# Revit family: ancoPLUS
name_source: partatom
category: Fixadores estruturais
revit_build: Autodesk Revit 2018 (Build: 20180423_1000(x64)
units: mm (PartAtom-declared; Revit-internal decimal feet)

## family parameters
Com base no plano de trabalho = Não
Compartilhado = Não
Corte com vazios quando carregada = Não
Sempre na vertical = Sim

## types (12) — shared parameters
Ancre_hauteur = 100  [stored 0.328084 ft]
Fers de montage inférieur = Sim
Fers de montage supérieur = Sim
LT1 = 1100
LT2 = 1050
Longueur fers de montage après dernière ancre = 100  [stored 0.328084 ft]
Material = Ancre
Nombre d’ancres = 10
Visibilidade_Acre_10 = Sim
Visibilidade_Acre_2 = Sim
Visibilidade_Acre_3 = Sim
Visibilidade_Acre_4 = Sim
Visibilidade_Acre_5 = Sim
Visibilidade_Acre_6 = Sim
Visibilidade_Acre_7 = Sim
Visibilidade_Acre_8 = Sim
Visibilidade_Acre_9 = Sim
XC1 = 100  [stored 0.328084 ft]
XC10 = 100  [stored 0.328084 ft]
XC2 = 100  [stored 0.328084 ft]
XC3 = 100  [stored 0.328084 ft]
XC4 = 100  [stored 0.328084 ft]
XC5 = 100  [stored 0.328084 ft]
XC6 = 100  [stored 0.328084 ft]
XC7 = 100  [stored 0.328084 ft]
XC8 = 100  [stored 0.328084 ft]
XC9 = 100  [stored 0.328084 ft]

## per-type parameters (varying)
| type | Ancre_Ø | Ancre_Ø/2 | Enrobage supérieure | H1 | H2 | H_T | Modelo | Ø | ØF | ØF_Posição_Horizontal | ØF_Posição_Vertical | ØT |
| DX | 10 | 5  [stored 0.0164042 ft] | 0  [stored 0 ft] | 3  [stored 0.00984252 ft] | 3  [stored 0.00984252 ft] | 88 | DX | 10  [stored 0.0328084 ft] | 6  [stored 0.019685 ft] | 9  [stored 0.0295276 ft] | 3  [stored 0.00984252 ft] | 15  [stored 0.0492126 ft] |
| DA | 12 | 6  [stored 0.019685 ft] | 80  [stored 0.262467 ft] | 3  [stored 0.00984252 ft] | 3  [stored 0.00984252 ft] | 87 | DA | 12  [stored 0.0393701 ft] | 6  [stored 0.019685 ft] | 9  [stored 0.0295276 ft] | 3  [stored 0.00984252 ft] | 18  [stored 0.0590551 ft] |
| DB | 14 | 7  [stored 0.0229659 ft] | 80  [stored 0.262467 ft] | 4  [stored 0.0131234 ft] | 4  [stored 0.0131234 ft] | 86  [stored 0.282152 ft] | DB | 14  [stored 0.0459318 ft] | 6  [stored 0.019685 ft] | 9  [stored 0.0295276 ft] | 3  [stored 0.00984252 ft] | 21  [stored 0.0688976 ft] |
| DC | 16 | 8  [stored 0.0262467 ft] | 80  [stored 0.262467 ft] | 4  [stored 0.0131234 ft] | 4  [stored 0.0131234 ft] | 86  [stored 0.282152 ft] | DC | 16  [stored 0.0524934 ft] | 8  [stored 0.0262467 ft] | 10  [stored 0.0328084 ft] | 4  [stored 0.0131234 ft] | 24  [stored 0.0787402 ft] |
| DG | 20 | 10  [stored 0.0328084 ft] | 80  [stored 0.262467 ft] | 4  [stored 0.0131234 ft] | 5  [stored 0.0164042 ft] | 82  [stored 0.269029 ft] | DG | 20  [stored 0.0656168 ft] | 9  [stored 0.0295276 ft] | 11  [stored 0.0360892 ft] | 5  [stored 0.0164042 ft] | 30  [stored 0.0984252 ft] |
| DJ | 22 | 11  [stored 0.0360892 ft] | 80  [stored 0.262467 ft] | 5  [stored 0.0164042 ft] | 6  [stored 0.019685 ft] | 80  [stored 0.262467 ft] | DJ | 22  [stored 0.0721785 ft] | 8  [stored 0.0262467 ft] | 10  [stored 0.0328084 ft] | 4  [stored 0.0131234 ft] | 33 |
| DO | 25 | 13 | 80  [stored 0.262467 ft] | 6  [stored 0.019685 ft] | 7  [stored 0.0229659 ft] | 74  [stored 0.242782 ft] | DO | 25  [stored 0.082021 ft] | 10  [stored 0.0328084 ft] | 11  [stored 0.0360892 ft] | 5  [stored 0.0164042 ft] | 38 |
| DN | 25 | 13 | 80  [stored 0.262467 ft] | 6  [stored 0.019685 ft] | 7  [stored 0.0229659 ft] | 74  [stored 0.242782 ft] | DO | 25  [stored 0.082021 ft] | 10  [stored 0.0328084 ft] | 11  [stored 0.0360892 ft] | 5  [stored 0.0164042 ft] | 38 |
| DP | 25 | 13 | 80  [stored 0.262467 ft] | 6  [stored 0.019685 ft] | 7  [stored 0.0229659 ft] | 74  [stored 0.242782 ft] | DO | 25  [stored 0.082021 ft] | 10  [stored 0.0328084 ft] | 11  [stored 0.0360892 ft] | 5  [stored 0.0164042 ft] | 38 |
| DT | 28 | 14  [stored 0.0459318 ft] | 80  [stored 0.262467 ft] | 7  [stored 0.0229659 ft] | 8  [stored 0.0262467 ft] | 70 | DT | 28  [stored 0.0918635 ft] | 10  [stored 0.0328084 ft] | 11  [stored 0.0360892 ft] | 5  [stored 0.0164042 ft] | 42  [stored 0.137795 ft] |
| DW | 28 | 14  [stored 0.0459318 ft] | 80  [stored 0.262467 ft] | 7  [stored 0.0229659 ft] | 8  [stored 0.0262467 ft] | 70 | DT | 28  [stored 0.0918635 ft] | 10  [stored 0.0328084 ft] | 11  [stored 0.0360892 ft] | 5  [stored 0.0164042 ft] | 42  [stored 0.137795 ft] |
| DU | 28 | 14  [stored 0.0459318 ft] | 80  [stored 0.262467 ft] | 7  [stored 0.0229659 ft] | 8  [stored 0.0262467 ft] | 70 | DT | 28  [stored 0.0918635 ft] | 10  [stored 0.0328084 ft] | 11  [stored 0.0360892 ft] | 5  [stored 0.0164042 ft] | 42  [stored 0.137795 ft] |

note: [stored X ft] marks values corroborated as IEEE doubles in the binary element streams (Revit-internal decimal feet)

## geometry (parser evidence)
native form markers: Sweep x2
no freeform markers — native parametric forms only
